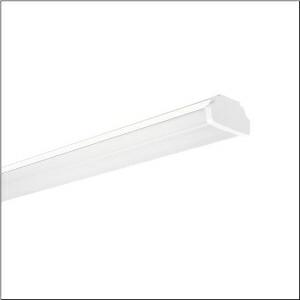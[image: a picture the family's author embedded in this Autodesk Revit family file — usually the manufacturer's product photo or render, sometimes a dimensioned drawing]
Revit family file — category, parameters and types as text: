
# Revit family: modario_r__31_gen_2_53bm812mv4g5d2_e2e8
name_source: partatom
category: Lighting Fixtures
units: mm (PartAtom-declared; Revit-internal decimal feet)

## family parameters
Cut with Voids When Loaded = No
Host = Face
Light Source = No
Part Type = Normal
Room Calculation Point = No
Round Connector Dimension = Use Diameter
Shared = No

## types (1)
- --- (1 x LED, 16690 lm, 89.8 W, 4000K)
    Apparent Load = 90 VA
    CIE Flux Codes = 47 80 95 93 100
    Color Rendering = 80
    Color Temperature = 4000K
    Default Elevation = 1800 mm
    Description = Modario® 31 Gen.2, luminaire insert, of sheet steel, coil coated, white, length: 1.495mm, width: 81mm, height: 82mm, 5x system unit, system units: 299mm, LED rated luminous flux: 16.690lm, light colour: 840, control gear: ON/OFF Multilumen, control gear: ECG, with plug, 3-pole, with phase selection, mains connection: 220..240V, AC, 50/60Hz, rated input power: 90W, through-wiring accessed according to module size, primary optical cover: cover, of PMMA, light emission: direct distribution, primary light characteristic: symmetric, protection rating (complete): IP20, protection rating (LED compartment): IP50, insulation class (complete): insulation class I (protective earthing), certification: CE, ENEC, VDE, UKCA, impact resistance: IK03, permissible ambient temperature for indoor applications: -35..+30°C, corresponds to IFS (International Featured Standards) requirements for safety and quality in the food industry, reducing of maximum allowable ambient temperature of 5°C with ceiling mounting, IP40 when using the optional accessory 5TP9018, packaging unit: 1 piece
    Height = 92 mm
    Lamp = 1 x LED
    Lamp Light Flux = 16690 lm
    Lamp Power = 89.8 W
    Lamp count = 1
    Length = 1495 mm
    Luminous efficacy = 186 lm/W
    Manufacturer = Siteco
    ModVariant = No
    Model = 53BM812MV4G5D2
    Mounting Place = Ceiling
    Mounting Type = Pendant
    Number of Poles = 1
    OnlyDefault = Yes
    Power Factor = 1
    Product Name = Modario® 31 Gen.2
    Product group = luminaire insert
    ProductGroupID = 902
    Protection Class = Protection class I
    Protection Degree = IP 20
    RLX_Detail_Level = 1
    RLX_Emergency_Light_Flux = 0 lm
    RLX_Emergency_Type = 0
    RLX_Emergency_Type_DB = No
    RlxData = <blob elided: 40057 chars, md5=c4b8f4f8>
    Socket = socket
    Standby Power = 0 W
    System Light Flux = 16690 lm
    System Power = 90 W
    Type Comments = factory setting: luminous flux: 100 % | (A | C | E) | 210 mA
    Type Image = l_1341886.jpg
    URL = http://relux.com
    VarID = @adj_043374
    Voltage = 0 V
    Weight = 0.00 kg
    Width = 81 mm

## geometry (parser evidence)
native form markers: Blend x4, Sweep x11
no freeform markers — native parametric forms only
